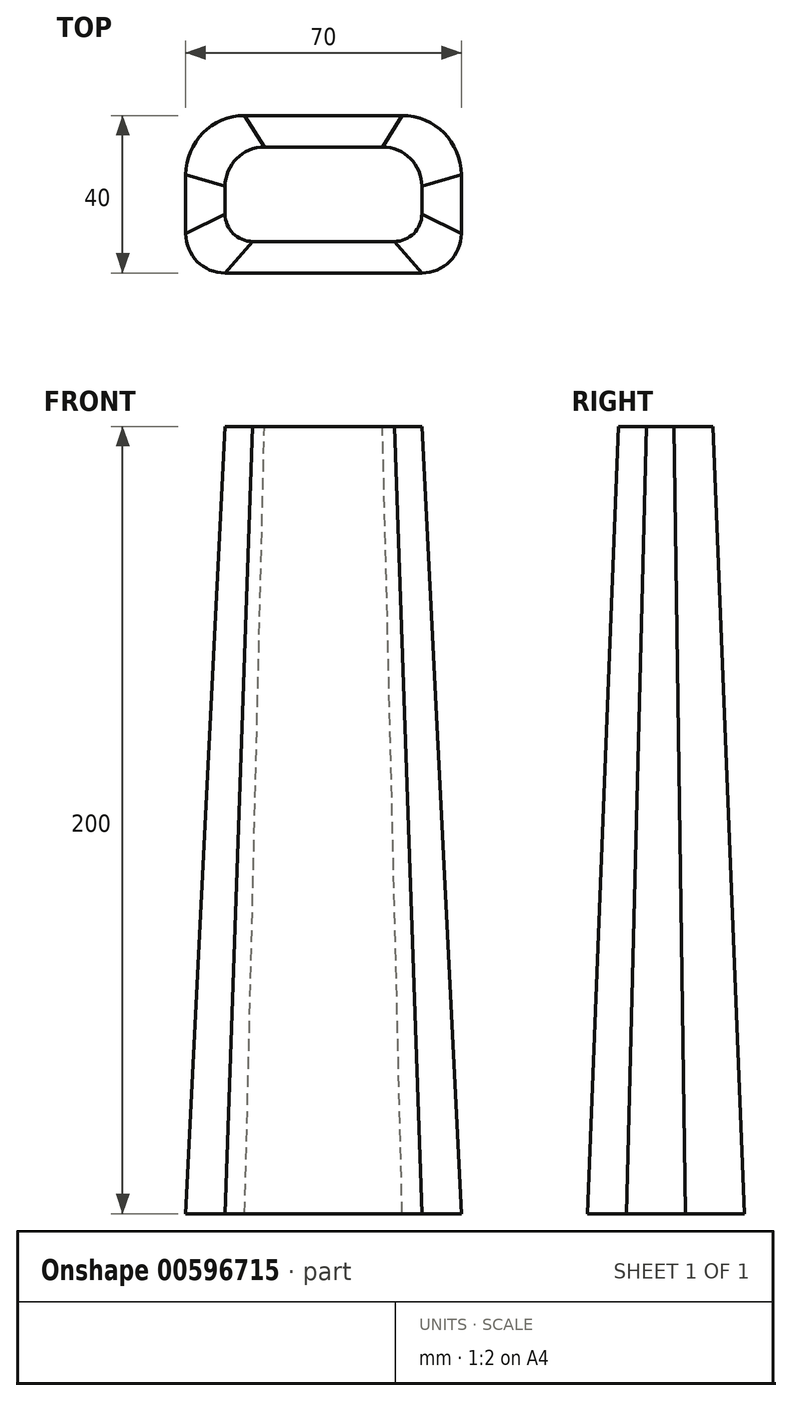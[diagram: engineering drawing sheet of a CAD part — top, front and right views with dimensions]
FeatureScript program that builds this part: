
annotation { "Feature Type Name" : "Feature", "Feature Type Description" : "" }
export const myFeature = defineFeature(function(context is Context, id is Id, definition is map)
    precondition{}
    {
        {
            var Q0;
            Q0=qCreatedBy(makeId("Top.planeOp"),FACE);
            var sketch = newSketch(context, id + "F0", { "sketchPlane" : qUnion([Q0])});
            skLineSegment(sketch, "E0.bottom", {"start": v(15, 12) * mm, "end": v(-15, 12) * mm});
            skLineSegment(sketch, "E0.top", {"start": v(18, -12) * mm, "end": v(-18, -12) * mm});
            skLineSegment(sketch, "E0.left", {"start": v(25, 2) * mm, "end": v(25, -5) * mm});
            skLineSegment(sketch, "E0.right", {"start": v(-25, 2) * mm, "end": v(-25, -5) * mm});
            skPoint(sketch, "E0.middle", {"position": v(0, 0) * mm});
            skPoint(sketch, "E1.visualSharp", {"position": v(-25, 12) * mm});
            skArc(sketch, "E1.filletArc", {"start": v(-15, 12) * mm, "mid": v(-22.07, 9.07) * mm, "end": v(-25, 2) * mm});
            skPoint(sketch, "E2.visualSharp", {"position": v(25, 12) * mm});
            skArc(sketch, "E2.filletArc", {"start": v(25, 2) * mm, "mid": v(22.07, 9.07) * mm, "end": v(15, 12) * mm});
            skPoint(sketch, "E3.visualSharp", {"position": v(-25, -12) * mm});
            skArc(sketch, "E3.filletArc", {"start": v(-25, -5) * mm, "mid": v(-22.95, -9.95) * mm, "end": v(-18, -12) * mm});
            skPoint(sketch, "E4.visualSharp", {"position": v(25, -12) * mm});
            skArc(sketch, "E4.filletArc", {"start": v(18, -12) * mm, "mid": v(22.95, -9.95) * mm, "end": v(25, -5) * mm});
            skSolve(sketch);
        }
        {
            var Q0;
            Q0=qCreatedBy(makeId("Top.planeOp"),FACE);
            cPlane(context, id + "F1", {"entities" : qUnion([Q0]), "cplaneType" : CPlaneType.OFFSET, "offset" : 200 * mm, "oppositeDirection" : true, "width" : 150 * mm, "height" : 150 * mm});
        }
        {
            var Q0;
            Q0=qCreatedBy(id+"F1.planeOp",FACE);
            var sketch = newSketch(context, id + "F2", { "sketchPlane" : qUnion([Q0])});
            skLineSegment(sketch, "E5.bottom", {"start": v(-20, 20) * mm, "end": v(20, 20) * mm});
            skLineSegment(sketch, "E5.top", {"start": v(-25, -20) * mm, "end": v(25, -20) * mm});
            skLineSegment(sketch, "E5.left", {"start": v(-35, 5) * mm, "end": v(-35, -10) * mm});
            skLineSegment(sketch, "E5.right", {"start": v(35, 5) * mm, "end": v(35, -10) * mm});
            skPoint(sketch, "E5.middle", {"position": v(0, 0) * mm});
            skPoint(sketch, "E6.visualSharp", {"position": v(35, 20) * mm});
            skArc(sketch, "E6.filletArc", {"start": v(35, 5) * mm, "mid": v(30.6, 15.6) * mm, "end": v(20, 20) * mm});
            skPoint(sketch, "E7.visualSharp", {"position": v(-35, 20) * mm});
            skArc(sketch, "E7.filletArc", {"start": v(-20, 20) * mm, "mid": v(-30.6, 15.6) * mm, "end": v(-35, 5) * mm});
            skPoint(sketch, "E8.visualSharp", {"position": v(35, -20) * mm});
            skArc(sketch, "E8.filletArc", {"start": v(25, -20) * mm, "mid": v(32.07, -17.07) * mm, "end": v(35, -10) * mm});
            skPoint(sketch, "E9.visualSharp", {"position": v(-35, -20) * mm});
            skArc(sketch, "E9.filletArc", {"start": v(-35, -10) * mm, "mid": v(-32.07, -17.07) * mm, "end": v(-25, -20) * mm});
            skSolve(sketch);
        }
        {
            var Q0;
            Q0=makeQuery(id+"F2.imprint","IMPRINT",FACE,{"disambiguationData":[TD([[makeQuery(id+"F2.imprint","IMPRINT",EDGE,{"derivedFrom":sQuery(id+"F2.wireOp",EDGE,"E5.bottom")}),-1.0]])]});
            var Q1;
            Q1=makeQuery(id+"F0.imprint","IMPRINT",FACE,{"disambiguationData":[TD([[makeQuery(id+"F0.imprint","IMPRINT",EDGE,{"derivedFrom":sQuery(id+"F0.wireOp",EDGE,"E0.bottom")}),1.0]])]});
            loft(context, id + "F3", {"sheetProfilesArray" : [{ "sheetProfileEntities" : qUnion([Q0]) }, { "sheetProfileEntities" : qUnion([Q1]) }]});
        }
    });
